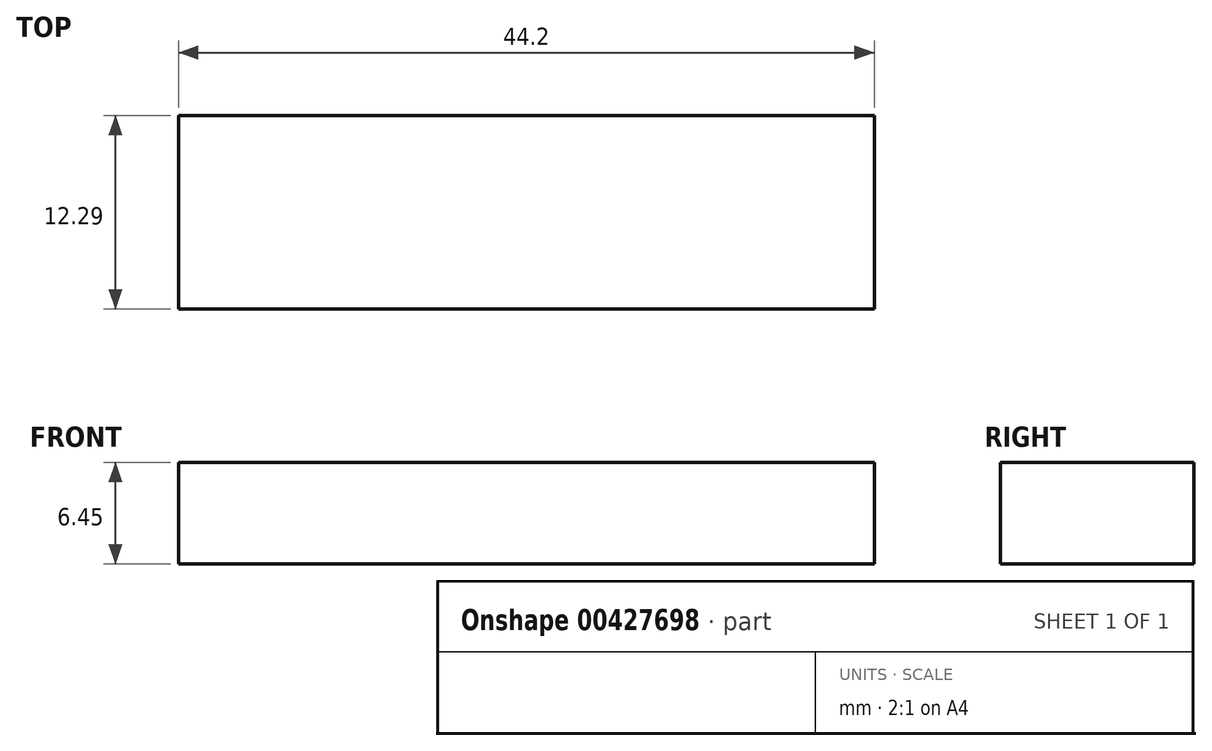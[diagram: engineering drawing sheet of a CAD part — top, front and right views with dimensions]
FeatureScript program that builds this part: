
annotation { "Feature Type Name" : "Feature", "Feature Type Description" : "" }
export const myFeature = defineFeature(function(context is Context, id is Id, definition is map)
    precondition{}
    {
        {
            var Q0;
            Q0=qCreatedBy(makeId("Top.planeOp"),FACE);
            var sketch = newSketch(context, id + "F0", { "sketchPlane" : qUnion([Q0])});
            skLineSegment(sketch, "E0.bottom", {"start": v(0, 0) * mm, "end": v(44.2, 0) * mm});
            skLineSegment(sketch, "E0.top", {"start": v(0, 12.3) * mm, "end": v(44.2, 12.3) * mm});
            skLineSegment(sketch, "E0.left", {"start": v(0, 0) * mm, "end": v(0, 12.3) * mm});
            skLineSegment(sketch, "E0.right", {"start": v(44.2, 0) * mm, "end": v(44.2, 12.3) * mm});
            skSolve(sketch);
        }
        {
            var Q0;
            Q0 = qSketchRegion(id + "F0", true);
            extrude(context, id + "F1", {"entities" : qUnion([Q0]), "depth" : 6.45 * mm});
        }
    });
